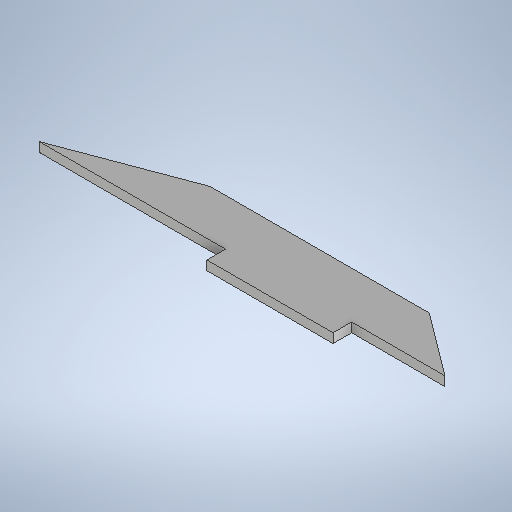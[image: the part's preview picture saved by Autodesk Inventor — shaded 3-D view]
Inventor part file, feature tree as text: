
AUTODESK INVENTOR PART (.ipt)
format: ipt  version: 2025.1 (Build 291241020, 241B)  size: 251,904 bytes
history: native  units: mm
features: extrude x1, sketch x1
ambient origin geometry x8: Origin, YZ Plane, XZ Plane, XY Plane, X Axis, Y Axis, Z Axis, Center Point
bodies: Solid1 (feature_tree)
feature tree (2):
  extrude  "Extrusion1"  Depth=6.0mm
  sketch  "Sketch1"  dims[d10=3.0mm d11=0.0mm d24=6.0mm d26=60.0mm d27=40.6mm d28=30.0mm d29=15.0mm d30=40.0mm d31=20.0mm]
